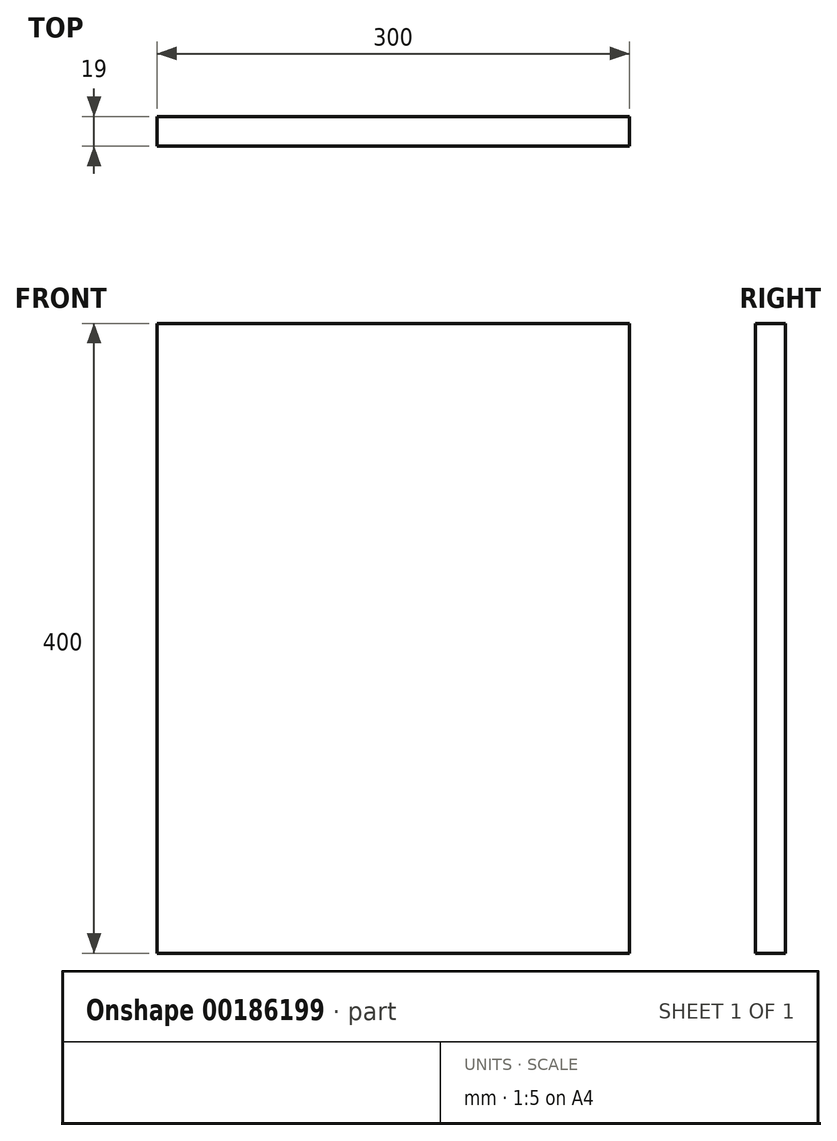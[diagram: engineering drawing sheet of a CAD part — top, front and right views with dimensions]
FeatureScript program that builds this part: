
annotation { "Feature Type Name" : "Feature", "Feature Type Description" : "" }
export const myFeature = defineFeature(function(context is Context, id is Id, definition is map)
    precondition{}
    {
        {
            var Q0;
            Q0=qCreatedBy(makeId("Front.planeOp"),FACE);
            var sketch = newSketch(context, id + "F0", { "sketchPlane" : qUnion([Q0])});
            skLineSegment(sketch, "E0.bottom", {"start": v(-149.37, 211.3) * mm, "end": v(150.63, 211.3) * mm});
            skLineSegment(sketch, "E0.top", {"start": v(-149.37, -188.7) * mm, "end": v(150.63, -188.7) * mm});
            skLineSegment(sketch, "E0.left", {"start": v(-149.37, 211.3) * mm, "end": v(-149.37, -188.7) * mm});
            skLineSegment(sketch, "E0.right", {"start": v(150.63, 211.3) * mm, "end": v(150.63, -188.7) * mm});
            skSolve(sketch);
        }
        {
            var Q0;
            Q0 = qSketchRegion(id + "F0", true);
            extrude(context, id + "F1", {"entities" : qUnion([Q0]), "depth" : 19 * mm});
        }
    });
